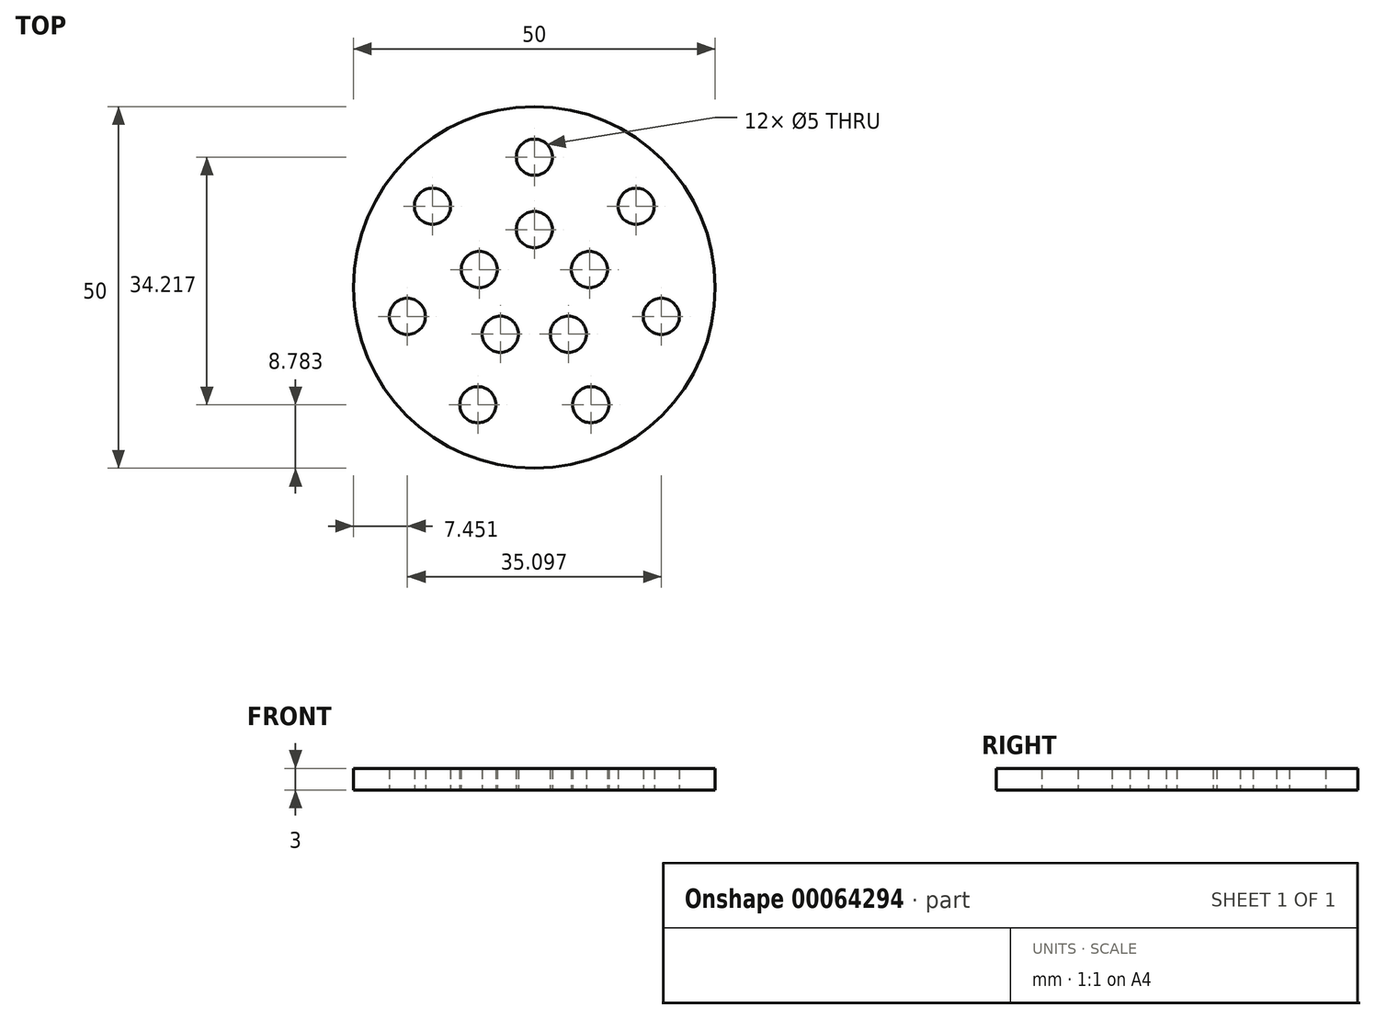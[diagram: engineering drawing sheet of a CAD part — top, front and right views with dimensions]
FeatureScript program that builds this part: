
annotation { "Feature Type Name" : "Feature", "Feature Type Description" : "" }
export const myFeature = defineFeature(function(context is Context, id is Id, definition is map)
    precondition{}
    {
        {
            var Q0;
            Q0=qCreatedBy(makeId("Top.planeOp"),FACE);
            var sketch = newSketch(context, id + "F0", { "sketchPlane" : qUnion([Q0])});
            skCircle(sketch, "E0", {"center": v(0, 0) * mm, "radius": 25 * mm});
            skCircle(sketch, "E1", {"center": v(0, 18) * mm, "radius": 2.5 * mm});
            skCircle(sketch, "E2.1.0", {"center": v(-14.07, 11.22) * mm, "radius": 2.5 * mm});
            skCircle(sketch, "E2.2.0", {"center": v(-17.55, -4) * mm, "radius": 2.5 * mm});
            skCircle(sketch, "E3.1.3.0", {"center": v(-7.8, -16.22) * mm, "radius": 2.5 * mm});
            skCircle(sketch, "E3.1.4.0", {"center": v(7.8, -16.22) * mm, "radius": 2.5 * mm});
            skCircle(sketch, "E4.1.5.0", {"center": v(17.55, -4) * mm, "radius": 2.5 * mm});
            skCircle(sketch, "E5.1.6.0", {"center": v(14.07, 11.22) * mm, "radius": 2.5 * mm});
            skCircle(sketch, "E6", {"center": v(0, 8) * mm, "radius": 2.5 * mm});
            skCircle(sketch, "E7.1.0", {"center": v(-7.6, 2.47) * mm, "radius": 2.5 * mm});
            skCircle(sketch, "E7.2.0", {"center": v(-4.7, -6.47) * mm, "radius": 2.5 * mm});
            skCircle(sketch, "E8.1.3.0", {"center": v(4.7, -6.47) * mm, "radius": 2.5 * mm});
            skCircle(sketch, "E8.1.4.0", {"center": v(7.6, 2.47) * mm, "radius": 2.5 * mm});
            skSolve(sketch);
        }
        {
            var Q0;
            Q0 = qSketchRegion(id + "F0", true);
            extrude(context, id + "F1", {"entities" : qUnion([Q0]), "depth" : 3 * mm});
        }
    });
